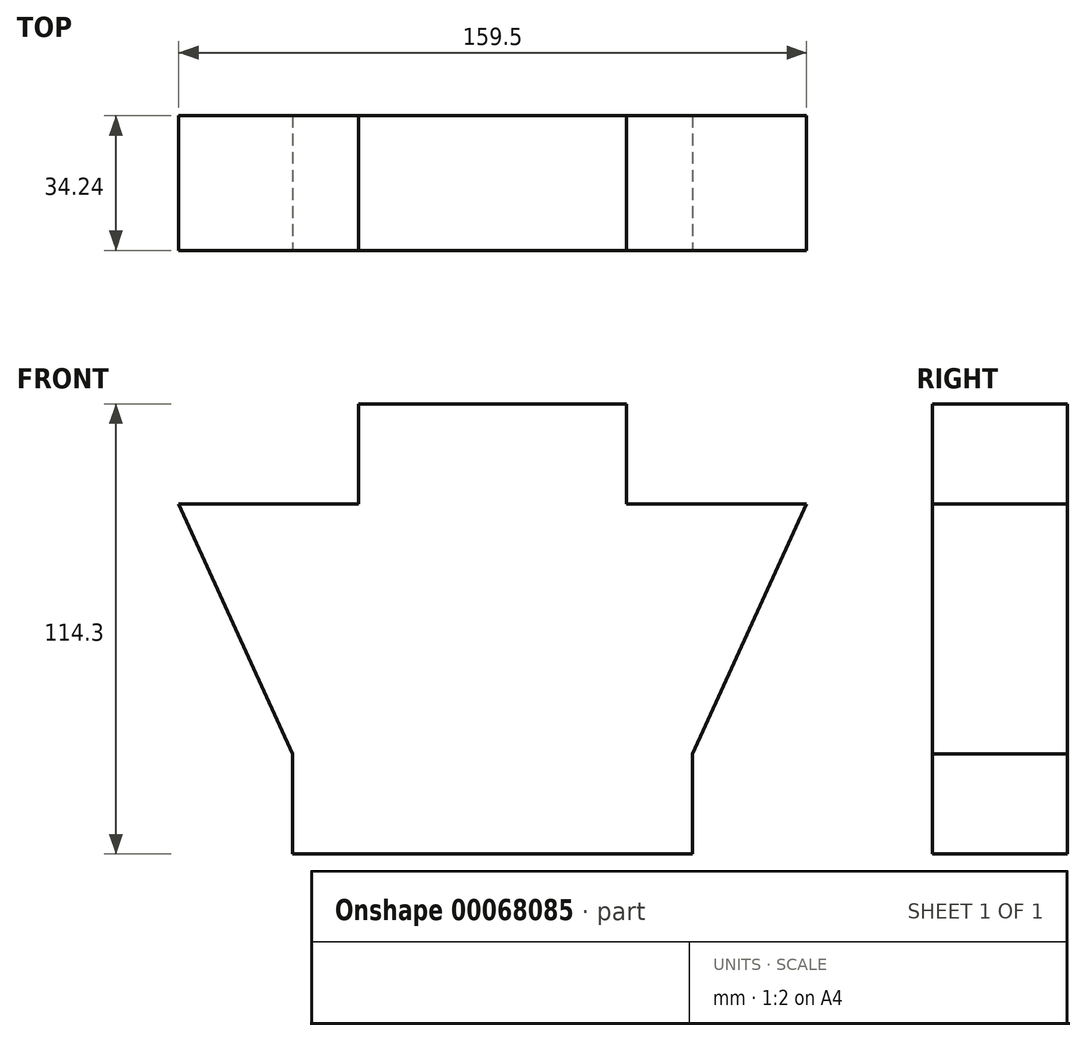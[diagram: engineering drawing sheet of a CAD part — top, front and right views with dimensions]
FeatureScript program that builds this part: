
annotation { "Feature Type Name" : "Feature", "Feature Type Description" : "" }
export const myFeature = defineFeature(function(context is Context, id is Id, definition is map)
    precondition{}
    {
        {
            var Q0;
            Q0=qCreatedBy(makeId("Front.planeOp"),FACE);
            var sketch = newSketch(context, id + "F0", { "sketchPlane" : qUnion([Q0])});
            skLineSegment(sketch, "E0", {"start": v(50.8, 0) * mm, "end": v(50.8, 25.4) * mm});
            skLineSegment(sketch, "E1", {"start": v(50.8, 25.4) * mm, "end": v(79.75, 88.9) * mm});
            skLineSegment(sketch, "E2", {"start": v(79.75, 88.9) * mm, "end": v(34.03, 88.9) * mm});
            skLineSegment(sketch, "E3", {"start": v(34.03, 88.9) * mm, "end": v(34.03, 114.3) * mm});
            skLineSegment(sketch, "E4", {"start": v(0, 0) * mm, "end": v(0, 114.3) * mm, "construction": true});
            skLineSegment(sketch, "E5", {"start": v(0, 114.3) * mm, "end": v(34.03, 114.3) * mm});
            skLineSegment(sketch, "E6", {"start": v(50.8, 0) * mm, "end": v(0, 0) * mm});
            skLineSegment(sketch, "E7", {"start": v(0, 79.92) * mm, "end": v(30.08, 79.92) * mm});
            skLineSegment(sketch, "E8", {"start": v(0, 49.57) * mm, "end": v(36.52, 49.57) * mm});
            skArc(sketch, "E9", {"start": v(36.52, 49.57) * mm, "mid": v(45.6, 67.35) * mm, "end": v(30.08, 79.92) * mm});
            skLineSegment(sketch, "E10.MirrorCS", {"start": v(0, 114.3) * mm, "end": v(-34.03, 114.3) * mm});
            skLineSegment(sketch, "E11.MirrorCS", {"start": v(-34.03, 88.9) * mm, "end": v(-34.03, 114.3) * mm});
            skLineSegment(sketch, "E12.MirrorCS", {"start": v(-79.75, 88.9) * mm, "end": v(-34.03, 88.9) * mm});
            skLineSegment(sketch, "E13.MirrorCS", {"start": v(-50.8, 25.4) * mm, "end": v(-79.75, 88.9) * mm});
            skLineSegment(sketch, "E14.MirrorCS", {"start": v(-50.8, 0) * mm, "end": v(-50.8, 25.4) * mm});
            skLineSegment(sketch, "E15.MirrorCS", {"start": v(-50.8, 0) * mm, "end": v(0, 0) * mm});
            skSolve(sketch);
        }
        {
            var Q0;
            Q0=makeQuery(id+"F0.imprint","IMPRINT",FACE,{"disambiguationData":[TD([[makeQuery(id+"F0.imprint","IMPRINT",EDGE,{"derivedFrom":sQuery(id+"F0.wireOp",EDGE,"E0")}),1.0]])]});
            extrude(context, id + "F1", {"entities" : qUnion([Q0]), "oppositeDirection" : true, "depth" : 34.24 * mm});
        }
    });
